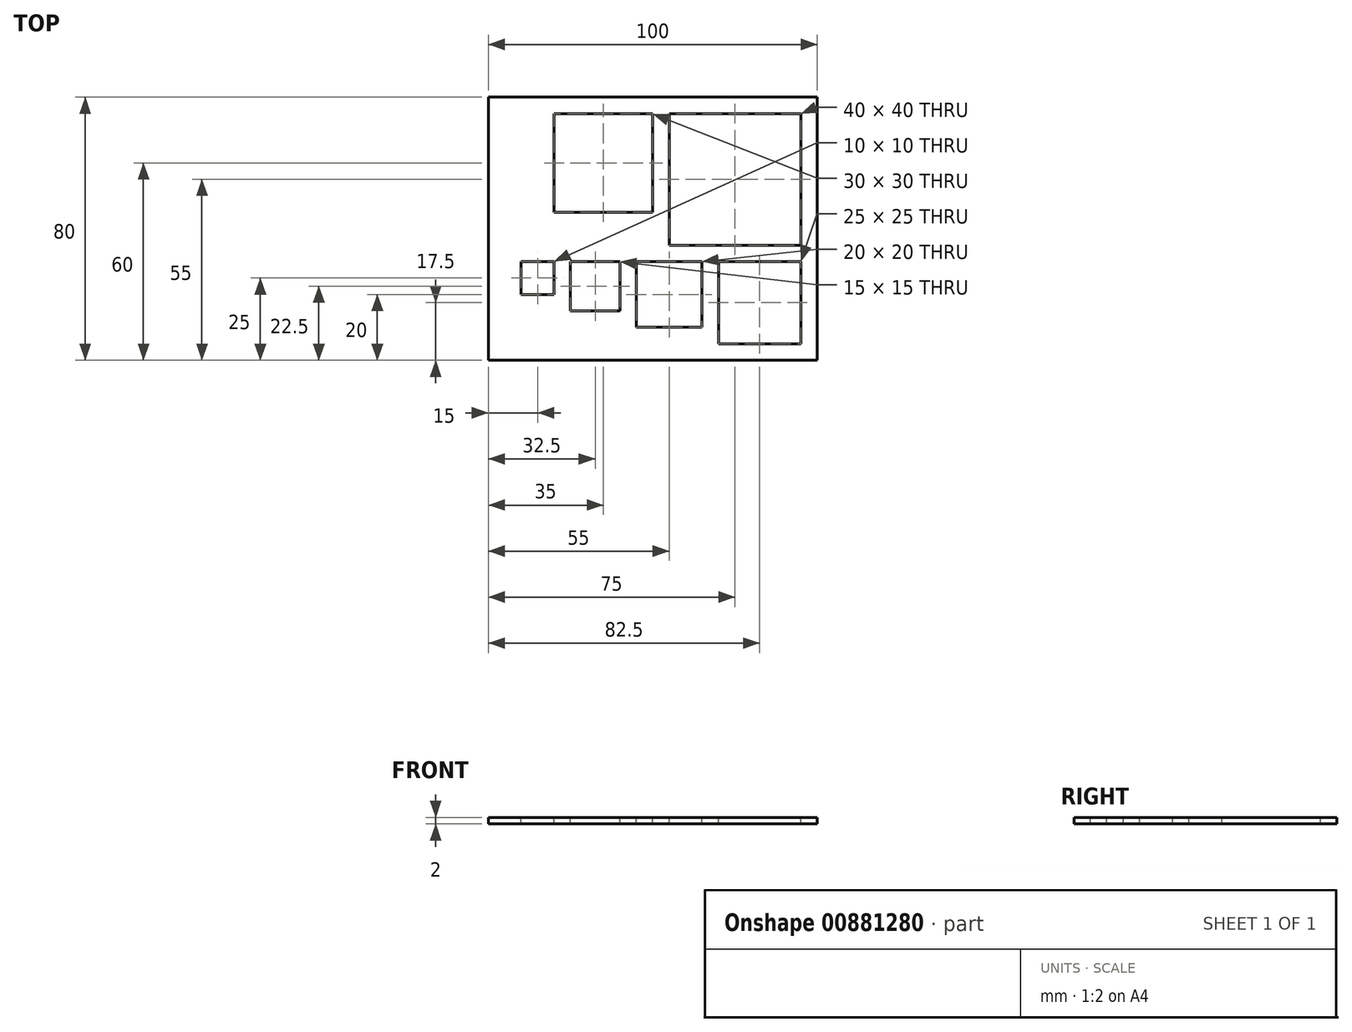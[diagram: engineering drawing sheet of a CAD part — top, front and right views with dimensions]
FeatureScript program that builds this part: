
annotation { "Feature Type Name" : "Feature", "Feature Type Description" : "" }
export const myFeature = defineFeature(function(context is Context, id is Id, definition is map)
    precondition{}
    {
        {
            var Q0;
            Q0=qCreatedBy(makeId("Top.planeOp"),FACE);
            var sketch = newSketch(context, id + "F0", { "sketchPlane" : qUnion([Q0])});
            skLineSegment(sketch, "E0.bottom", {"start": v(0, 0) * mm, "end": v(100, 0) * mm});
            skLineSegment(sketch, "E0.top", {"start": v(0, 80) * mm, "end": v(100, 80) * mm});
            skLineSegment(sketch, "E0.left", {"start": v(0, 0) * mm, "end": v(0, 80) * mm});
            skLineSegment(sketch, "E0.right", {"start": v(100, 0) * mm, "end": v(100, 80) * mm});
            skSolve(sketch);
        }
        {
            var Q0;
            Q0 = qSketchRegion(id + "F0", true);
            extrude(context, id + "F1", {"entities" : qUnion([Q0]), "depth" : 2 * mm, "offsetDistance" : 25 * mm});
        }
        {
            var Q0;
            Q0=makeQuery(id+"F1.opExtrude","CAP_FACE",FACE,{"disambiguationData":[OSD([sQuery(id+"F0.wireOp",EDGE,"E0.bottom"),sQuery(id+"F0.wireOp",EDGE,"E0.top"),sQuery(id+"F0.wireOp",EDGE,"E0.left"),sQuery(id+"F0.wireOp",EDGE,"E0.right")])],"isStart":false});
            var sketch = newSketch(context, id + "F2", { "sketchPlane" : qUnion([Q0])});
            skLineSegment(sketch, "E1.bottom", {"start": v(95, 75) * mm, "end": v(55, 75) * mm});
            skLineSegment(sketch, "E1.top", {"start": v(95, 35) * mm, "end": v(55, 35) * mm});
            skLineSegment(sketch, "E1.left", {"start": v(95, 75) * mm, "end": v(95, 35) * mm});
            skLineSegment(sketch, "E1.right", {"start": v(55, 75) * mm, "end": v(55, 35) * mm});
            skLineSegment(sketch, "E2.bottom", {"start": v(50, 75) * mm, "end": v(20, 75) * mm});
            skLineSegment(sketch, "E2.top", {"start": v(50, 45) * mm, "end": v(20, 45) * mm});
            skLineSegment(sketch, "E2.left", {"start": v(50, 75) * mm, "end": v(50, 45) * mm});
            skLineSegment(sketch, "E2.right", {"start": v(20, 75) * mm, "end": v(20, 45) * mm});
            skLineSegment(sketch, "E3.bottom", {"start": v(95, 30) * mm, "end": v(70, 30) * mm});
            skLineSegment(sketch, "E3.top", {"start": v(95, 5) * mm, "end": v(70, 5) * mm});
            skLineSegment(sketch, "E3.left", {"start": v(95, 30) * mm, "end": v(95, 5) * mm});
            skLineSegment(sketch, "E3.right", {"start": v(70, 30) * mm, "end": v(70, 5) * mm});
            skLineSegment(sketch, "E4.bottom", {"start": v(65, 30) * mm, "end": v(45, 30) * mm});
            skLineSegment(sketch, "E4.top", {"start": v(65, 10) * mm, "end": v(45, 10) * mm});
            skLineSegment(sketch, "E4.left", {"start": v(65, 30) * mm, "end": v(65, 10) * mm});
            skLineSegment(sketch, "E4.right", {"start": v(45, 30) * mm, "end": v(45, 10) * mm});
            skLineSegment(sketch, "E5.bottom", {"start": v(40, 30) * mm, "end": v(25, 30) * mm});
            skLineSegment(sketch, "E5.top", {"start": v(40, 15) * mm, "end": v(25, 15) * mm});
            skLineSegment(sketch, "E5.left", {"start": v(40, 30) * mm, "end": v(40, 15) * mm});
            skLineSegment(sketch, "E5.right", {"start": v(25, 30) * mm, "end": v(25, 15) * mm});
            skLineSegment(sketch, "E6.bottom", {"start": v(20, 30) * mm, "end": v(10, 30) * mm});
            skLineSegment(sketch, "E6.top", {"start": v(20, 20) * mm, "end": v(10, 20) * mm});
            skLineSegment(sketch, "E6.left", {"start": v(20, 30) * mm, "end": v(20, 20) * mm});
            skLineSegment(sketch, "E6.right", {"start": v(10, 30) * mm, "end": v(10, 20) * mm});
            skSolve(sketch);
        }
        {
            var Q0;
            Q0 = qSketchRegion(id + "F2", true);
            extrude(context, id + "F3", {"entities" : qUnion([Q0]), "operationType" : NewBodyOperationType.REMOVE, "endBound" : BoundingType.THROUGH_ALL, "oppositeDirection" : true, "depth" : 25 * mm, "offsetDistance" : 25 * mm});
        }
    });
